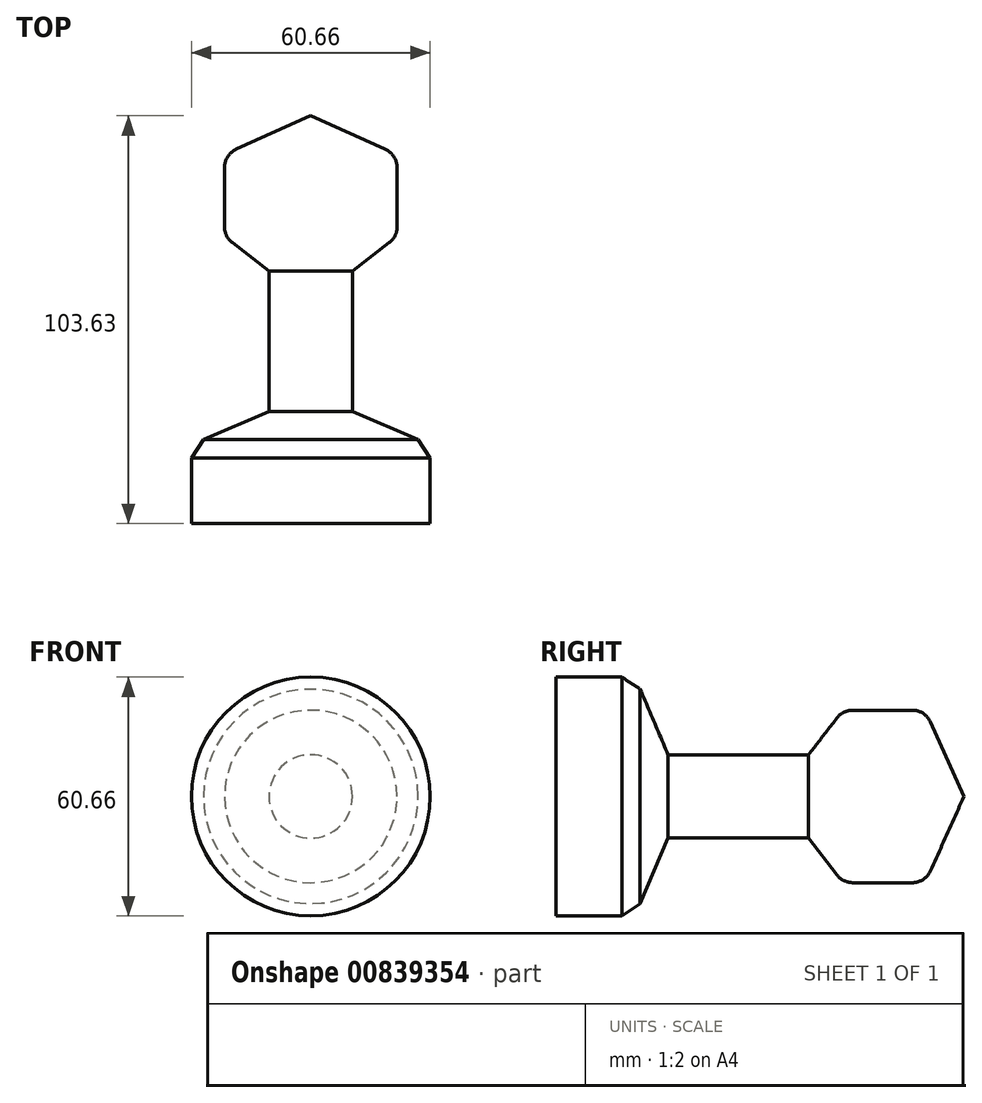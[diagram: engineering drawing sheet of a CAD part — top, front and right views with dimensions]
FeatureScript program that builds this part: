
annotation { "Feature Type Name" : "Feature", "Feature Type Description" : "" }
export const myFeature = defineFeature(function(context is Context, id is Id, definition is map)
    precondition{}
    {
        {
            var Q0;
            Q0=qCreatedBy(makeId("Right.planeOp"),FACE);
            var sketch = newSketch(context, id + "F0", { "sketchPlane" : qUnion([Q0])});
            skLineSegment(sketch, "E0", {"start": v(69.8, 0) * mm, "end": v(-61.97, 0) * mm, "construction": true});
            skLineSegment(sketch, "E1", {"start": v(46, 0) * mm, "end": v(36.14, 21.91) * mm});
            skLineSegment(sketch, "E2", {"start": v(36.14, 21.91) * mm, "end": v(15.24, 21.91) * mm});
            skLineSegment(sketch, "E3", {"start": v(15.24, 21.91) * mm, "end": v(6.53, 10.6) * mm});
            skLineSegment(sketch, "E4", {"start": v(6.53, 10.6) * mm, "end": v(-29.17, 10.6) * mm});
            skLineSegment(sketch, "E5", {"start": v(-29.17, 10.6) * mm, "end": v(-37.59, 30.33) * mm});
            skLineSegment(sketch, "E6", {"start": v(-37.59, 30.33) * mm, "end": v(-57.62, 30.33) * mm});
            skLineSegment(sketch, "E7", {"start": v(-57.62, 30.33) * mm, "end": v(-57.62, 0) * mm});
            skLineSegment(sketch, "E8", {"start": v(-57.62, 0) * mm, "end": v(46, 0) * mm});
            skSolve(sketch);
        }
        {
            var Q0;
            Q0 = qSketchRegion(id + "F0", true);
            var Q1;
            Q1=sQuery(id+"F0.wireOp",EDGE,"E0");
            revolve(context, id + "F1", {"surfaceOperationType" : NewSurfaceOperationType.NEW, "entities" : qUnion([Q0]), "axis" : qUnion([Q1]), "revolveType" : RevolveType.FULL});
        }
        {
            var Q0;
            Q0=makeQuery(id+"F1.opRevolve","SWEPT_EDGE",EDGE,{"disambiguationData":[OSD([sQuery(id+"F0.wireOp",EDGE,"E1"),sQuery(id+"F0.wireOp",EDGE,"E2")])]});
            var Q1;
            Q1=makeQuery(id+"F1.opRevolve","SWEPT_EDGE",EDGE,{"disambiguationData":[OSD([sQuery(id+"F0.wireOp",EDGE,"E2"),sQuery(id+"F0.wireOp",EDGE,"E3")])]});
            fillet(context, id + "F2", {"entities" : qUnion([Q0, Q1]), "radius" : 5.08 * mm, "tangentPropagation" : true, "allowEdgeOverflow" : false});
        }
        {
            var Q0;
            Q0=makeQuery(id+"F1.opRevolve","SWEPT_EDGE",EDGE,{"disambiguationData":[OSD([sQuery(id+"F0.wireOp",EDGE,"E5"),sQuery(id+"F0.wireOp",EDGE,"E6")])]});
            chamfer(context, id + "F3", {"entities" : qUnion([Q0]), "width" : 5.08 * mm, "tangentPropagation" : true});
        }
    });
